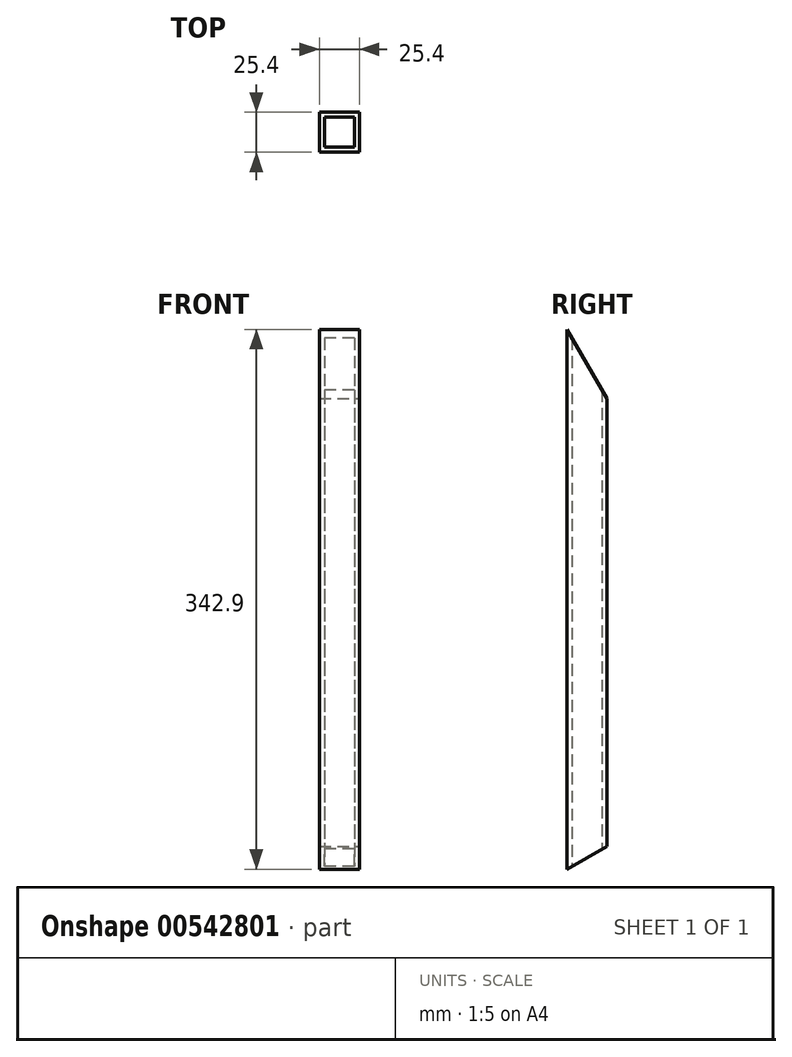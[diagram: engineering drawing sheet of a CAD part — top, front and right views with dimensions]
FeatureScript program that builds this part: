
annotation { "Feature Type Name" : "Feature", "Feature Type Description" : "" }
export const myFeature = defineFeature(function(context is Context, id is Id, definition is map)
    precondition{}
    {
        {
            var Q0;
            Q0=qCreatedBy(makeId("Top.planeOp"),FACE);
            var sketch = newSketch(context, id + "F0", { "sketchPlane" : qUnion([Q0])});
            skLineSegment(sketch, "E0.bottom", {"start": v(-25.4, 25.4) * mm, "end": v(0, 25.4) * mm});
            skLineSegment(sketch, "E0.top", {"start": v(-25.4, 0) * mm, "end": v(0, 0) * mm});
            skLineSegment(sketch, "E0.left", {"start": v(-25.4, 25.4) * mm, "end": v(-25.4, 0) * mm});
            skLineSegment(sketch, "E0.right", {"start": v(0, 25.4) * mm, "end": v(0, 0) * mm});
            skLineSegment(sketch, "E1.bottom", {"start": v(-22.23, 22.22) * mm, "end": v(-3.17, 22.22) * mm});
            skLineSegment(sketch, "E1.top", {"start": v(-22.22, 3.18) * mm, "end": v(-3.17, 3.18) * mm});
            skLineSegment(sketch, "E1.left", {"start": v(-22.23, 22.22) * mm, "end": v(-22.22, 3.18) * mm});
            skLineSegment(sketch, "E1.right", {"start": v(-3.17, 22.22) * mm, "end": v(-3.17, 3.18) * mm});
            skSolve(sketch);
        }
        {
            var Q0;
            Q0=makeQuery(id+"F0.imprint","IMPRINT",FACE,{"disambiguationData":[TD([[makeQuery(id+"F0.imprint","IMPRINT",EDGE,{"derivedFrom":sQuery(id+"F0.wireOp",EDGE,"E0.bottom")}),-1.0]])]});
            extrude(context, id + "F1", {"entities" : qUnion([Q0]), "depth" : 342.9 * mm, "offsetDistance" : 25.4 * mm});
        }
        {
            var Q0;
            Q0=makeQuery(id+"F1.opExtrude","SWEPT_FACE",FACE,{"disambiguationData":[OSD([sQuery(id+"F0.wireOp",EDGE,"E0.right")])]});
            var sketch = newSketch(context, id + "F2", { "sketchPlane" : qUnion([Q0])});
            skLineSegment(sketch, "E2", {"start": v(0, 0) * mm, "end": v(25.4, 0) * mm});
            skLineSegment(sketch, "E3", {"start": v(0, 0) * mm, "end": v(25.4, 14.66) * mm});
            skLineSegment(sketch, "E4", {"start": v(25.4, 14.66) * mm, "end": v(25.4, 0) * mm});
            skLineSegment(sketch, "E5", {"start": v(25.4, 342.9) * mm, "end": v(0, 342.9) * mm});
            skLineSegment(sketch, "E6", {"start": v(0, 342.9) * mm, "end": v(25.4, 298.9) * mm});
            skLineSegment(sketch, "E7", {"start": v(25.4, 298.9) * mm, "end": v(25.4, 342.9) * mm});
            skSolve(sketch);
        }
        {
            var Q0;
            Q0=makeQuery(id+"F2.imprint","IMPRINT",FACE,{"disambiguationData":[TD([[makeQuery(id+"F2.imprint","IMPRINT",EDGE,{"derivedFrom":sQuery(id+"F2.wireOp",EDGE,"E5")}),1.0]])]});
            var Q1;
            Q1=makeQuery(id+"F2.imprint","IMPRINT",FACE,{"disambiguationData":[TD([[makeQuery(id+"F2.imprint","IMPRINT",EDGE,{"derivedFrom":sQuery(id+"F2.wireOp",EDGE,"E2")}),-1.0]])]});
            extrude(context, id + "F3", {"entities" : qUnion([Q0, Q1]), "operationType" : NewBodyOperationType.REMOVE, "oppositeDirection" : true, "depth" : 25.4 * mm, "offsetDistance" : 25.4 * mm});
        }
    });
